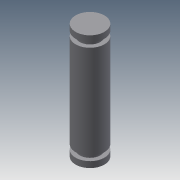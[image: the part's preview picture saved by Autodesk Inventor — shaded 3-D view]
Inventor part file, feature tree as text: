
AUTODESK INVENTOR PART (.ipt)
format: ipt  version: 2013 (Build 170138000, 138)  size: 85,504 bytes
history: native  units: mm
features: revolve x1, sketch x1
ambient origin geometry x8: Origin, YZ Plane, XZ Plane, XY Plane, X Axis, Y Axis, Z Axis, Center Point
bodies: Solid1 (feature_tree)
feature tree (2):
  revolve  "Revolution1"  [1 undecoded]
  sketch  "Sketch1"  dims[d12=19.5mm d13=1.0mm d14=0.85mm d16=1.0mm d17=90.0deg]
note: 1 required parameter value undecoded (feature->parameter linkage not recoverable at this tier; creation-order binding heuristic only, values carry confidence <= 0.55)
